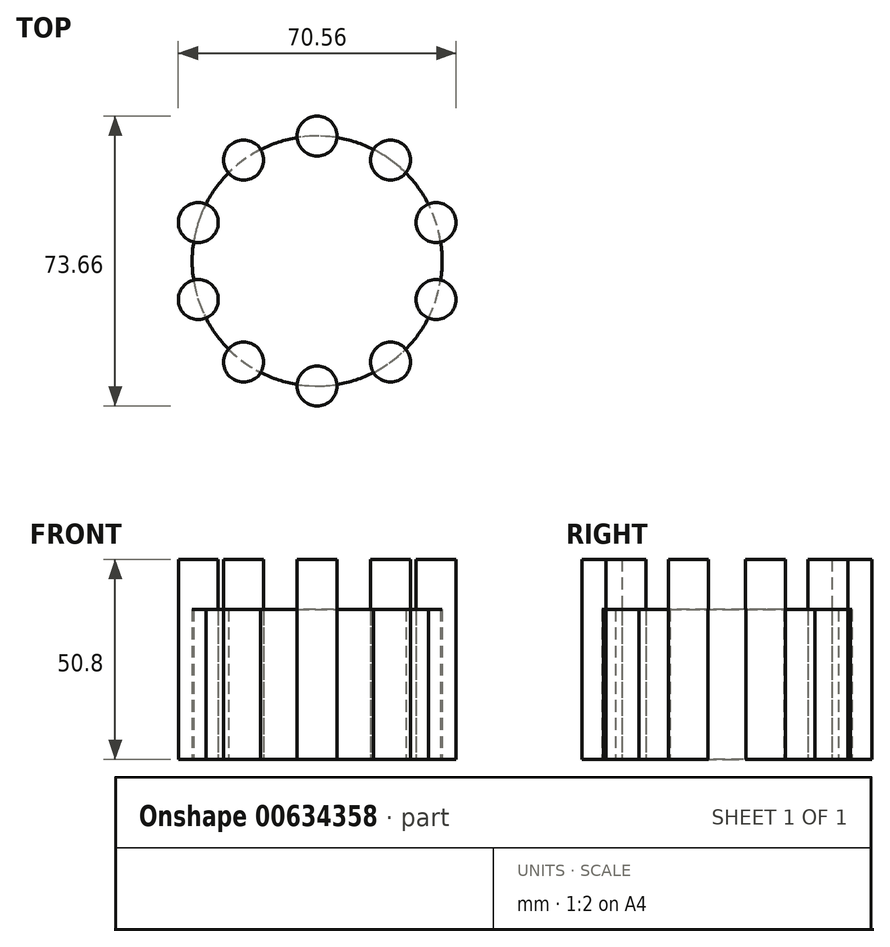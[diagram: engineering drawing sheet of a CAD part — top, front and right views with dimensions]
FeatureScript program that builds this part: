
annotation { "Feature Type Name" : "Feature", "Feature Type Description" : "" }
export const myFeature = defineFeature(function(context is Context, id is Id, definition is map)
    precondition{}
    {
        {
            var Q0;
            Q0=qCreatedBy(makeId("Top.planeOp"),FACE);
            var sketch = newSketch(context, id + "F0", { "sketchPlane" : qUnion([Q0])});
            skCircle(sketch, "E0", {"center": v(0, 0) * mm, "radius": 31.75 * mm});
            skSolve(sketch);
        }
        {
            var Q0;
            Q0=qSketchRegion(id+"F0",true);
            extrude(context, id + "F1", {"entities" : qUnion([Q0]), "depth" : 38.1 * mm});
        }
        {
            var Q0;
            Q0=qCreatedBy(makeId("Top.planeOp"),FACE);
            var sketch = newSketch(context, id + "F2", { "sketchPlane" : qUnion([Q0])});
            skCircle(sketch, "E1", {"center": v(0, 31.75) * mm, "radius": 5.08 * mm});
            skCircle(sketch, "E2.1.0", {"center": v(-18.66, 25.69) * mm, "radius": 5.08 * mm});
            skCircle(sketch, "E2.2.0", {"center": v(-30.2, 9.81) * mm, "radius": 5.08 * mm});
            skCircle(sketch, "E2.3.0", {"center": v(-30.2, -9.81) * mm, "radius": 5.08 * mm});
            skCircle(sketch, "E2.4.0", {"center": v(-18.66, -25.69) * mm, "radius": 5.08 * mm});
            skCircle(sketch, "E2.5.0", {"center": v(0, -31.75) * mm, "radius": 5.08 * mm});
            skCircle(sketch, "E2.6.0", {"center": v(18.66, -25.69) * mm, "radius": 5.08 * mm});
            skCircle(sketch, "E2.7.0", {"center": v(30.2, -9.81) * mm, "radius": 5.08 * mm});
            skCircle(sketch, "E2.8.0", {"center": v(30.2, 9.81) * mm, "radius": 5.08 * mm});
            skCircle(sketch, "E2.9.0", {"center": v(18.66, 25.69) * mm, "radius": 5.08 * mm});
            skPoint(sketch, "E2.center", {"position": v(0, 0) * mm});
            skSolve(sketch);
        }
        {
            var Q0;
            Q0=qSketchRegion(id+"F2",true);
            extrude(context, id + "F3", {"entities" : qUnion([Q0]), "depth" : 50.8 * mm});
        }
        {
            var Q0;
            Q0=makeQuery(id+"F1.opExtrude","SWEPT_BODY",BODY,{"disambiguationData":[OSD([sQuery(id+"F0.wireOp",EDGE,"E0")])]});
            var Q1;
            Q1=makeQuery(id+"F3.opExtrude","SWEPT_BODY",BODY,{"disambiguationData":[OSD([sQuery(id+"F2.wireOp",EDGE,"E1")])]});
            var Q2;
            Q2=makeQuery(id+"F3.opExtrude","SWEPT_BODY",BODY,{"disambiguationData":[OSD([sQuery(id+"F2.wireOp",EDGE,"E2.1.0")])]});
            var Q3;
            Q3=makeQuery(id+"F3.opExtrude","SWEPT_BODY",BODY,{"disambiguationData":[OSD([sQuery(id+"F2.wireOp",EDGE,"E2.2.0")])]});
            var Q4;
            Q4=makeQuery(id+"F3.opExtrude","SWEPT_BODY",BODY,{"disambiguationData":[OSD([sQuery(id+"F2.wireOp",EDGE,"E2.3.0")])]});
            var Q5;
            Q5=makeQuery(id+"F3.opExtrude","SWEPT_BODY",BODY,{"disambiguationData":[OSD([sQuery(id+"F2.wireOp",EDGE,"E2.4.0")])]});
            var Q6;
            Q6=makeQuery(id+"F3.opExtrude","SWEPT_BODY",BODY,{"disambiguationData":[OSD([sQuery(id+"F2.wireOp",EDGE,"E2.5.0")])]});
            var Q7;
            Q7=makeQuery(id+"F3.opExtrude","SWEPT_BODY",BODY,{"disambiguationData":[OSD([sQuery(id+"F2.wireOp",EDGE,"E2.6.0")])]});
            var Q8;
            Q8=makeQuery(id+"F3.opExtrude","SWEPT_BODY",BODY,{"disambiguationData":[OSD([sQuery(id+"F2.wireOp",EDGE,"E2.7.0")])]});
            var Q9;
            Q9=makeQuery(id+"F3.opExtrude","SWEPT_BODY",BODY,{"disambiguationData":[OSD([sQuery(id+"F2.wireOp",EDGE,"E2.8.0")])]});
            var Q10;
            Q10=makeQuery(id+"F3.opExtrude","SWEPT_BODY",BODY,{"disambiguationData":[OSD([sQuery(id+"F2.wireOp",EDGE,"E2.9.0")])]});
            booleanBodies(context, id + "F4", {"operationType" : BooleanOperationType.INTERSECTION, "tools" : qUnion([Q0, Q1, Q2, Q3, Q4, Q5, Q6, Q7, Q8, Q9, Q10]), "keepTools" : true});
        }
        {
            var Q0;
            Q0=makeQuery(id+"F3.opExtrude","SWEPT_BODY",BODY,{"disambiguationData":[OSD([sQuery(id+"F2.wireOp",EDGE,"E2.5.0")])]});
            var Q1;
            Q1=makeQuery(id+"F1.opExtrude","SWEPT_BODY",BODY,{"disambiguationData":[OSD([sQuery(id+"F0.wireOp",EDGE,"E0")])]});
            booleanBodies(context, id + "F5", {"operationType" : BooleanOperationType.INTERSECTION, "tools" : qUnion([Q0, Q1]), "keepTools" : true});
        }
        {
            var Q0;
            Q0=makeQuery(id+"F3.opExtrude","SWEPT_BODY",BODY,{"disambiguationData":[OSD([sQuery(id+"F2.wireOp",EDGE,"E2.6.0")])]});
            var Q1;
            Q1=makeQuery(id+"F1.opExtrude","SWEPT_BODY",BODY,{"disambiguationData":[OSD([sQuery(id+"F0.wireOp",EDGE,"E0")])]});
            booleanBodies(context, id + "F6", {"operationType" : BooleanOperationType.INTERSECTION, "tools" : qUnion([Q0, Q1]), "keepTools" : true});
        }
        {
            var Q0;
            Q0=makeQuery(id+"F1.opExtrude","SWEPT_BODY",BODY,{"disambiguationData":[OSD([sQuery(id+"F0.wireOp",EDGE,"E0")])]});
            var Q1;
            Q1=makeQuery(id+"F3.opExtrude","SWEPT_BODY",BODY,{"disambiguationData":[OSD([sQuery(id+"F2.wireOp",EDGE,"E2.7.0")])]});
            booleanBodies(context, id + "F7", {"operationType" : BooleanOperationType.INTERSECTION, "tools" : qUnion([Q0, Q1]), "keepTools" : true});
        }
        {
            var Q0;
            Q0=makeQuery(id+"F1.opExtrude","SWEPT_BODY",BODY,{"disambiguationData":[OSD([sQuery(id+"F0.wireOp",EDGE,"E0")])]});
            var Q1;
            Q1=makeQuery(id+"F3.opExtrude","SWEPT_BODY",BODY,{"disambiguationData":[OSD([sQuery(id+"F2.wireOp",EDGE,"E2.8.0")])]});
            booleanBodies(context, id + "F8", {"operationType" : BooleanOperationType.INTERSECTION, "tools" : qUnion([Q0, Q1]), "keepTools" : true});
        }
        {
            var Q0;
            Q0=makeQuery(id+"F1.opExtrude","SWEPT_BODY",BODY,{"disambiguationData":[OSD([sQuery(id+"F0.wireOp",EDGE,"E0")])]});
            var Q1;
            Q1=makeQuery(id+"F3.opExtrude","SWEPT_BODY",BODY,{"disambiguationData":[OSD([sQuery(id+"F2.wireOp",EDGE,"E2.9.0")])]});
            booleanBodies(context, id + "F9", {"operationType" : BooleanOperationType.INTERSECTION, "tools" : qUnion([Q0, Q1]), "keepTools" : true});
        }
        {
            var Q0;
            Q0=makeQuery(id+"F3.opExtrude","SWEPT_BODY",BODY,{"disambiguationData":[OSD([sQuery(id+"F2.wireOp",EDGE,"E1")])]});
            var Q1;
            Q1=makeQuery(id+"F1.opExtrude","SWEPT_BODY",BODY,{"disambiguationData":[OSD([sQuery(id+"F0.wireOp",EDGE,"E0")])]});
            booleanBodies(context, id + "F10", {"operationType" : BooleanOperationType.INTERSECTION, "tools" : qUnion([Q0, Q1]), "keepTools" : true});
        }
        {
            var Q0;
            Q0=makeQuery(id+"F3.opExtrude","SWEPT_BODY",BODY,{"disambiguationData":[OSD([sQuery(id+"F2.wireOp",EDGE,"E2.1.0")])]});
            var Q1;
            Q1=makeQuery(id+"F1.opExtrude","SWEPT_BODY",BODY,{"disambiguationData":[OSD([sQuery(id+"F0.wireOp",EDGE,"E0")])]});
            booleanBodies(context, id + "F11", {"operationType" : BooleanOperationType.INTERSECTION, "tools" : qUnion([Q0, Q1]), "keepTools" : true});
        }
        {
            var Q0;
            Q0=makeQuery(id+"F3.opExtrude","SWEPT_BODY",BODY,{"disambiguationData":[OSD([sQuery(id+"F2.wireOp",EDGE,"E2.2.0")])]});
            var Q1;
            Q1=makeQuery(id+"F1.opExtrude","SWEPT_BODY",BODY,{"disambiguationData":[OSD([sQuery(id+"F0.wireOp",EDGE,"E0")])]});
            booleanBodies(context, id + "F12", {"operationType" : BooleanOperationType.INTERSECTION, "tools" : qUnion([Q0, Q1]), "keepTools" : true});
        }
        {
            var Q0;
            Q0=makeQuery(id+"F3.opExtrude","SWEPT_BODY",BODY,{"disambiguationData":[OSD([sQuery(id+"F2.wireOp",EDGE,"E2.3.0")])]});
            var Q1;
            Q1=makeQuery(id+"F1.opExtrude","SWEPT_BODY",BODY,{"disambiguationData":[OSD([sQuery(id+"F0.wireOp",EDGE,"E0")])]});
            booleanBodies(context, id + "F13", {"operationType" : BooleanOperationType.INTERSECTION, "tools" : qUnion([Q0, Q1]), "keepTools" : true});
        }
        {
            var Q0;
            Q0=makeQuery(id+"F3.opExtrude","SWEPT_BODY",BODY,{"disambiguationData":[OSD([sQuery(id+"F2.wireOp",EDGE,"E2.4.0")])]});
            var Q1;
            Q1=makeQuery(id+"F1.opExtrude","SWEPT_BODY",BODY,{"disambiguationData":[OSD([sQuery(id+"F0.wireOp",EDGE,"E0")])]});
            booleanBodies(context, id + "F14", {"operationType" : BooleanOperationType.INTERSECTION, "tools" : qUnion([Q0, Q1]), "keepTools" : true});
        }
    });
